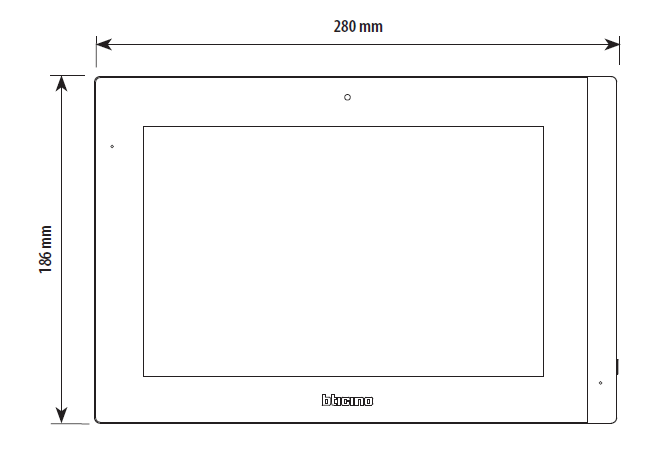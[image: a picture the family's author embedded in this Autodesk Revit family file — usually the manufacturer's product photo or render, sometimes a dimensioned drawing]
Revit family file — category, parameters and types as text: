
# Revit family: Bticino-Door Entry System-Classe 300EOS-Internal Unit
name_source: partatom
category: Equipement électrique
units: mm (PartAtom-declared; Revit-internal decimal feet)

## family parameters
Configuration du panneau = Deux colonnes, circuits au sein
Cote de connecteur circulaire = Utiliser le diamètre
Couper avec des vides une fois chargée = Non
Hôte = Face
Partagée = Non
Point de calcul de pièce = Non
Type d'élément = Tableau de raccordement

## types (2) — shared parameters
Camera = Without camera
Color = White
Configurator website = https://www.homesystems-legrandgroup.com
Connected Object = Oui
Connection type = bus system
Depth = 32 mm  [stored 0.104987 ft]
Door open button = Oui
Elévation par défaut = 1100 mm
General Conditions of Use = https://export.legrand.com
Height = 222 mm
IP = 54
Installation method = surface
Interface type = Wi-Fi/ RJ45
L3 = 115 mm  [stored 0.377297 ft]
Operating temperature MIN-MAX = +5/+40 °C
Screen Size (Inch) = 5
Screen resolution = 1280x720
Tension = 20-27 V DC
Touchscreen = Oui
Width = 121 mm  [stored 0.396982 ft]
With video = Oui

## per-type parameters (varying)
| type | Compatible with hearing aid | Reference | Teleloop |
| CLASSE 300EOS WITH NETATMO (Alexa integrated) | Non | BT-344842 | Non |
| CLASSE 300EOS WITH NETATMO TELELOOP  (Alexa integrated) | Oui | BT-344845 | Oui |

note: column(s) folded — value = type name in every type: Product designation

note: [stored X ft] marks values corroborated as IEEE doubles in the binary element streams (Revit-internal decimal feet)
